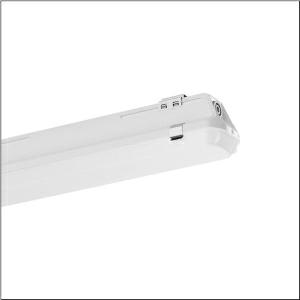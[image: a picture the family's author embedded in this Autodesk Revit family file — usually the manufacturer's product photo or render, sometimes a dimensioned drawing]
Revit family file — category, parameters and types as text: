
# Revit family: monsun_r__11_parking_51fg20dp440h_7f6a
name_source: partatom
category: Lighting Fixtures
units: mm (PartAtom-declared; Revit-internal decimal feet)

## family parameters
Cut with Voids When Loaded = No
Host = Face
Light Source = No
Part Type = Normal
Room Calculation Point = No
Round Connector Dimension = Use Diameter
Shared = No

## types (1)
- --- (1 x LED, 4840 lm, 30.8 W, 4000K)
    Apparent Load = 31 VA
    CIE Flux Codes = 45 75 93 94 100
    Color Rendering = 80
    Color Temperature = 4000K
    Default Elevation = 1800 mm
    Description = Monsun® 11 parking, damp-proof luminaire, chain hanger, primary optical cover: enclosure, of PC, light emission: direct distribution, primary light characteristic: symmetric, installation type: suspended mounting, surface-mounted, horizontal mounting, vertical mounting, LED, rated luminous flux: 4.840lm, luminous efficacy: 157lm/W, light colour: 840, colour temperature: 4000K, control gear: ECG DALI, with terminal, 5-pole, max. 2.5mm², mains connection: 220..240V, AC, 50/60Hz, rated input power: 31W, housing, of glass-fibre reinforced polyester, uncoated, bright grey, incl. chain hanger, length: 1.590mm, width: 90mm, height: 88mm, clip for enclosure, of stainless steel (V2A), ceiling mounting element, of stainless steel (V2A), chain hanger, of stainless steel (V2A), protection rating (complete): IP66, insulation class (complete): insulation class I (protective earthing), certification: CE, ENEC, VDE, UKCA, protection symbol: D, impact resistance: IK08, permissible operating ambient temperature: -25..+40°C, standard: EN 50419, EN 60598-2-1, no direct snow, no direct sun, no direct rain, for indoor or canopied outdoor use, corresponds to IFS (International Featured Standards) requirements for safety and quality in the food industry, contact your sales advisor before using the luminaires in applications with unclear chemical exposure, large temperature fluctuations or condensation-forming humidity, LABS conformity tested according to VDMA 24364:2018-05, packaging unit: 1 piece
    Height = 89 mm
    Lamp = 1 x LED
    Lamp Light Flux = 4840 lm
    Lamp Power = 30.8 W
    Lamp count = 1
    Length = 1590 mm
    Luminous efficacy = 157 lm/W
    Manufacturer = Siteco
    ModVariant = No
    Model = 51FG20DP440H
    Mounting Place = Ceiling
    Mounting Type = Surface mounted
    Number of Poles = 1
    OnlyDefault = Yes
    Power Factor = 1
    Product Name = Monsun® 11 parking
    Product group = damp-proof luminaire
    ProductGroupID = 300
    Protection Class = Protection class I
    Protection Degree = IP 66
    RLX_Detail_Level = 1
    RLX_Emergency_Light_Flux = 0 lm
    RLX_Emergency_Type = 0
    RLX_Emergency_Type_DB = No
    RlxData = <blob elided: 91953 chars, md5=1570e223>
    Socket = socket
    Standby Power = 0 W
    System Light Flux = 4840 lm
    System Power = 31 W
    Type Comments = factory setting: luminous flux: 100 % | dim-lin: 254 | 205 mA
    Type Image = l_1004748.jpg
    URL = http://relux.com
    VarID = @adj_140377
    Voltage = 0 V
    Weight = 0.00 kg
    Width = 90 mm

## geometry (parser evidence)
native form markers: Blend x4, Sweep x13
no freeform markers — native parametric forms only
